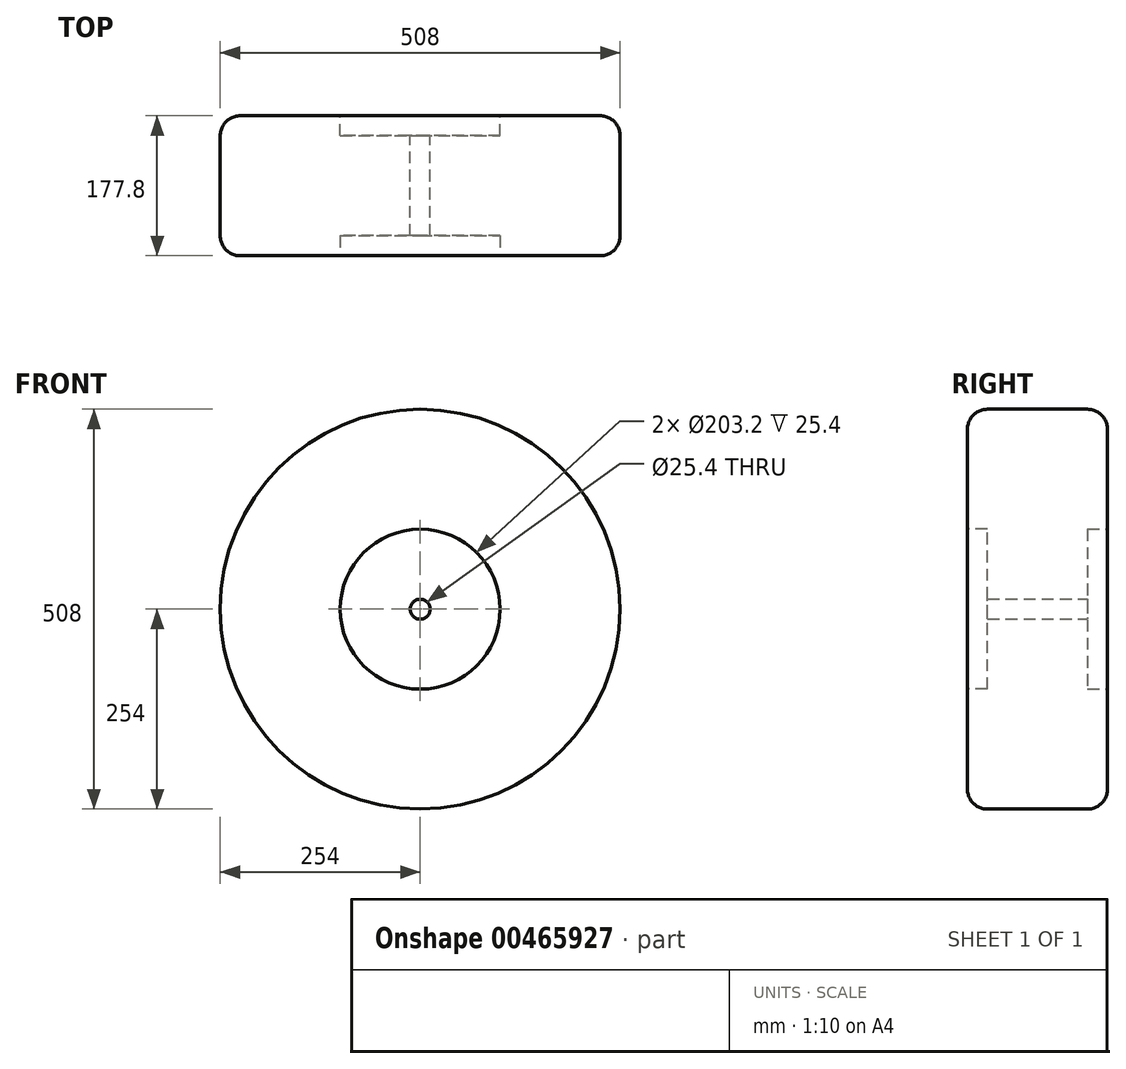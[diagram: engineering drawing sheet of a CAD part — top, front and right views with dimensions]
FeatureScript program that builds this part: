
annotation { "Feature Type Name" : "Feature", "Feature Type Description" : "" }
export const myFeature = defineFeature(function(context is Context, id is Id, definition is map)
    precondition{}
    {
        {
            var Q0;
            Q0=qCreatedBy(makeId("Front.planeOp"),FACE);
            var sketch = newSketch(context, id + "F0", { "sketchPlane" : qUnion([Q0])});
            skCircle(sketch, "E0", {"center": v(0, 0) * mm, "radius": 254 * mm});
            skSolve(sketch);
        }
        {
            var Q0;
            Q0=makeQuery(id+"F0.imprint","IMPRINT",FACE,{"disambiguationData":[TD([[makeQuery(id+"F0.imprint","IMPRINT",EDGE,{"derivedFrom":sQuery(id+"F0.wireOp",EDGE,"E0")}),1.0]])]});
            extrude(context, id + "F1", {"entities" : qUnion([Q0]), "endBound" : BoundingType.SYMMETRIC, "depth" : 177.8 * mm});
        }
        {
            var Q0;
            Q0=makeQuery(id+"F1.opExtrude","CAP_FACE",FACE,{"disambiguationData":[OSD([sQuery(id+"F0.wireOp",EDGE,"E0")])],"isStart":false});
            var sketch = newSketch(context, id + "F2", { "sketchPlane" : qUnion([Q0])});
            skCircle(sketch, "E1", {"center": v(0, 0) * mm, "radius": 101.6 * mm});
            skSolve(sketch);
        }
        {
            var Q0;
            Q0=makeQuery(id+"F2.imprint","IMPRINT",FACE,{"disambiguationData":[TD([[makeQuery(id+"F2.imprint","IMPRINT",EDGE,{"derivedFrom":sQuery(id+"F2.wireOp",EDGE,"E1")}),1.0]])]});
            extrude(context, id + "F3", {"entities" : qUnion([Q0]), "operationType" : NewBodyOperationType.REMOVE, "oppositeDirection" : true, "depth" : 25.4 * mm});
        }
        {
            var Q0;
            Q0=makeQuery(id+"F1.opExtrude","CAP_FACE",FACE,{"disambiguationData":[OSD([sQuery(id+"F0.wireOp",EDGE,"E0")])],"isStart":true});
            var sketch = newSketch(context, id + "F4", { "sketchPlane" : qUnion([Q0])});
            skCircle(sketch, "E2", {"center": v(0, 0) * mm, "radius": 101.6 * mm});
            skSolve(sketch);
        }
        {
            var Q0;
            Q0=makeQuery(id+"F4.imprint","IMPRINT",FACE,{"disambiguationData":[TD([[makeQuery(id+"F4.imprint","IMPRINT",EDGE,{"derivedFrom":sQuery(id+"F4.wireOp",EDGE,"E2")}),1.0]])]});
            extrude(context, id + "F5", {"entities" : qUnion([Q0]), "operationType" : NewBodyOperationType.REMOVE, "oppositeDirection" : true, "depth" : 25.4 * mm});
        }
        {
            var Q0;
            Q0=makeQuery(id+"F1.opExtrude","CAP_FACE",FACE,{"disambiguationData":[OSD([sQuery(id+"F0.wireOp",EDGE,"E0")])],"isStart":true});
            var sketch = newSketch(context, id + "F6", { "sketchPlane" : qUnion([Q0])});
            skCircle(sketch, "E3", {"center": v(0, 0) * mm, "radius": 12.7 * mm});
            skSolve(sketch);
        }
        {
            var Q0;
            Q0=makeQuery(id+"F6.imprint","IMPRINT",FACE,{"disambiguationData":[TD([[makeQuery(id+"F6.imprint","IMPRINT",EDGE,{"derivedFrom":sQuery(id+"F6.wireOp",EDGE,"E3")}),1.0]])]});
            extrude(context, id + "F7", {"entities" : qUnion([Q0]), "operationType" : NewBodyOperationType.REMOVE, "oppositeDirection" : true, "depth" : 127 * mm});
        }
        {
            var Q0;
            Q0=makeQuery(id+"F5.boolean.opBoolean","COPY",FACE,{"derivedFrom":makeQuery(id+"F5.opExtrude","CAP_FACE",FACE,{"disambiguationData":[OSD([sQuery(id+"F4.wireOp",EDGE,"E2")])],"isStart":false})});
            var sketch = newSketch(context, id + "F8", { "sketchPlane" : qUnion([Q0])});
            skCircle(sketch, "E4", {"center": v(0, 0) * mm, "radius": 12.7 * mm});
            skSolve(sketch);
        }
        {
            var Q0;
            Q0=makeQuery(id+"F8.imprint","IMPRINT",FACE,{"disambiguationData":[TD([[makeQuery(id+"F8.imprint","IMPRINT",EDGE,{"derivedFrom":sQuery(id+"F8.wireOp",EDGE,"E4")}),1.0]])]});
            extrude(context, id + "F9", {"entities" : qUnion([Q0]), "operationType" : NewBodyOperationType.REMOVE, "endBound" : BoundingType.SYMMETRIC, "depth" : 355.6 * mm});
        }
        {
            var Q0;
            Q0=makeQuery(id+"F1.opExtrude","CAP_EDGE",EDGE,{"disambiguationData":[OSD([sQuery(id+"F0.wireOp",EDGE,"E0")])],"isStart":false});
            var Q1;
            Q1=makeQuery(id+"F1.opExtrude","CAP_EDGE",EDGE,{"disambiguationData":[OSD([sQuery(id+"F0.wireOp",EDGE,"E0")])],"isStart":true});
            fillet(context, id + "F10", {"entities" : qUnion([Q0, Q1]), "radius" : 25.4 * mm, "tangentPropagation" : true, "allowEdgeOverflow" : false});
        }
    });
